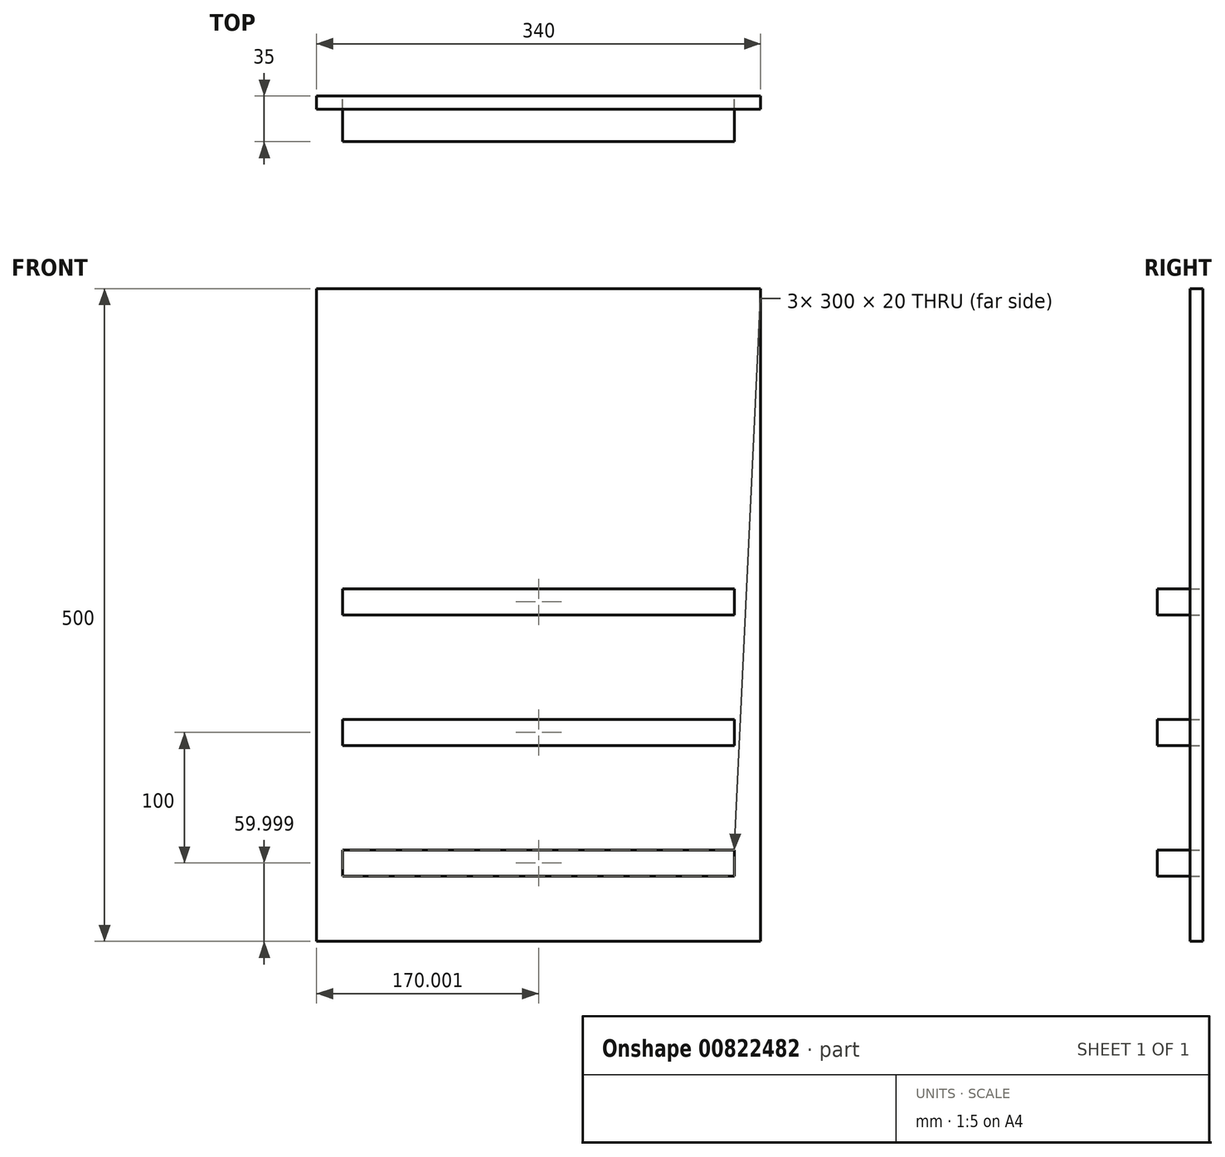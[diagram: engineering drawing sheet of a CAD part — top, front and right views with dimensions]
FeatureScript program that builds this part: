
annotation { "Feature Type Name" : "Feature", "Feature Type Description" : "" }
export const myFeature = defineFeature(function(context is Context, id is Id, definition is map)
    precondition{}
    {
        {
            var Q0;
            Q0=qCreatedBy(makeId("Front.planeOp"),FACE);
            var sketch = newSketch(context, id + "F0", { "sketchPlane" : qUnion([Q0])});
            skLineSegment(sketch, "E0.bottom", {"start": v(-224.23, 310.7) * mm, "end": v(115.77, 310.7) * mm});
            skLineSegment(sketch, "E0.top", {"start": v(-224.23, -189.3) * mm, "end": v(115.77, -189.3) * mm});
            skLineSegment(sketch, "E0.left", {"start": v(-224.23, 310.7) * mm, "end": v(-224.23, -189.3) * mm});
            skLineSegment(sketch, "E0.right", {"start": v(115.77, 310.7) * mm, "end": v(115.77, -189.3) * mm});
            skLineSegment(sketch, "E1.bottom", {"start": v(95.77, 80.7) * mm, "end": v(-204.23, 80.7) * mm});
            skLineSegment(sketch, "E1.top", {"start": v(95.77, 60.7) * mm, "end": v(-204.23, 60.7) * mm});
            skLineSegment(sketch, "E1.left", {"start": v(95.77, 80.7) * mm, "end": v(95.77, 60.7) * mm});
            skLineSegment(sketch, "E1.right", {"start": v(-204.23, 80.7) * mm, "end": v(-204.23, 60.7) * mm});
            skLineSegment(sketch, "E2.bottom", {"start": v(95.77, -19.3) * mm, "end": v(-204.23, -19.3) * mm});
            skLineSegment(sketch, "E2.top", {"start": v(95.77, -39.3) * mm, "end": v(-204.23, -39.3) * mm});
            skLineSegment(sketch, "E2.left", {"start": v(95.77, -19.3) * mm, "end": v(95.77, -39.3) * mm});
            skLineSegment(sketch, "E2.right", {"start": v(-204.23, -19.3) * mm, "end": v(-204.23, -39.3) * mm});
            skLineSegment(sketch, "E3.bottom", {"start": v(95.77, -119.3) * mm, "end": v(-204.23, -119.3) * mm});
            skLineSegment(sketch, "E3.top", {"start": v(95.77, -139.3) * mm, "end": v(-204.23, -139.3) * mm});
            skLineSegment(sketch, "E3.left", {"start": v(95.77, -119.3) * mm, "end": v(95.77, -139.3) * mm});
            skLineSegment(sketch, "E3.right", {"start": v(-204.23, -119.3) * mm, "end": v(-204.23, -139.3) * mm});
            skSolve(sketch);
        }
        {
            var Q0;
            Q0=makeQuery(id+"F0.imprint","IMPRINT",FACE,{"disambiguationData":[TD([[makeQuery(id+"F0.imprint","IMPRINT",EDGE,{"derivedFrom":sQuery(id+"F0.wireOp",EDGE,"E0.bottom")}),-1.0]])]});
            var Q1;
            {var subQ0=sQuery(id+"F0.wireOp",EDGE,"EU8g6nCk-4h4i-6KWV-wLJa-znDu51hTYt9s");Q1=makeQuery(id+"F0.imprint","IMPRINT",FACE,{"disambiguationData":[TD([[makeQuery(id+"F0.imprint","IMPRINT",EDGE,{"derivedFrom":subQ0}),1.0]])]});}
            var Q2;
            {var subQ0=sQuery(id+"F0.wireOp",EDGE,"DASBUczg-brEp-FSI8-lCjd-sA4li7qy1QZj");Q2=makeQuery(id+"F0.imprint","IMPRINT",FACE,{"disambiguationData":[TD([[makeQuery(id+"F0.imprint","IMPRINT",EDGE,{"derivedFrom":subQ0}),1.0]])]});}
            var Q3;
            {var subQ0=sQuery(id+"F0.wireOp",EDGE,"E0.top");Q3=makeQuery(id+"F0.imprint","IMPRINT",FACE,{"disambiguationData":[TD([[makeQuery(id+"F0.imprint","IMPRINT",EDGE,{"derivedFrom":subQ0}),1.0]])]});}
            extrude(context, id + "F1", {"entities" : qUnion([Q0, Q1, Q2, Q3]), "depth" : 10 * mm, "offsetDistance" : 25.4 * mm});
        }
        {
            var Q0;
            Q0=makeQuery(id+"F0.imprint","IMPRINT",FACE,{"disambiguationData":[TD([[makeQuery(id+"F0.imprint","IMPRINT",EDGE,{"derivedFrom":sQuery(id+"F0.wireOp",EDGE,"jTAJay3x-bNNf-MfL7-hyMn-WV2pMshx63SI")}),-1.0]])]});
            var Q1;
            Q1=makeQuery(id+"F0.imprint","IMPRINT",FACE,{"disambiguationData":[TD([[makeQuery(id+"F0.imprint","IMPRINT",EDGE,{"derivedFrom":sQuery(id+"F0.wireOp",EDGE,"f7LPRf9G-jyvK-sxHB-ZPQN-DSNNYYZH6BE5")}),-1.0]])]});
            var Q2;
            Q2=makeQuery(id+"F0.imprint","IMPRINT",FACE,{"disambiguationData":[TD([[makeQuery(id+"F0.imprint","IMPRINT",EDGE,{"derivedFrom":sQuery(id+"F0.wireOp",EDGE,"W6U1dGdo-AOVN-If1B-mSxN-zuEqJJkoPtOF")}),-1.0]])]});
            var Q3;
            Q3=makeQuery(id+"F0.imprint","IMPRINT",FACE,{"disambiguationData":[TD([[makeQuery(id+"F0.imprint","IMPRINT",EDGE,{"derivedFrom":sQuery(id+"F0.wireOp",EDGE,"E1.bottom")}),1.0]])]});
            var Q4;
            Q4=makeQuery(id+"F0.imprint","IMPRINT",FACE,{"disambiguationData":[TD([[makeQuery(id+"F0.imprint","IMPRINT",EDGE,{"derivedFrom":sQuery(id+"F0.wireOp",EDGE,"E2.bottom")}),1.0]])]});
            var Q5;
            Q5=makeQuery(id+"F0.imprint","IMPRINT",FACE,{"disambiguationData":[TD([[makeQuery(id+"F0.imprint","IMPRINT",EDGE,{"derivedFrom":sQuery(id+"F0.wireOp",EDGE,"E3.bottom")}),1.0]])]});
            extrude(context, id + "F2", {"entities" : qUnion([Q0, Q1, Q2, Q3, Q4, Q5]), "depth" : 35 * mm, "offsetDistance" : 25 * mm});
        }
    });
